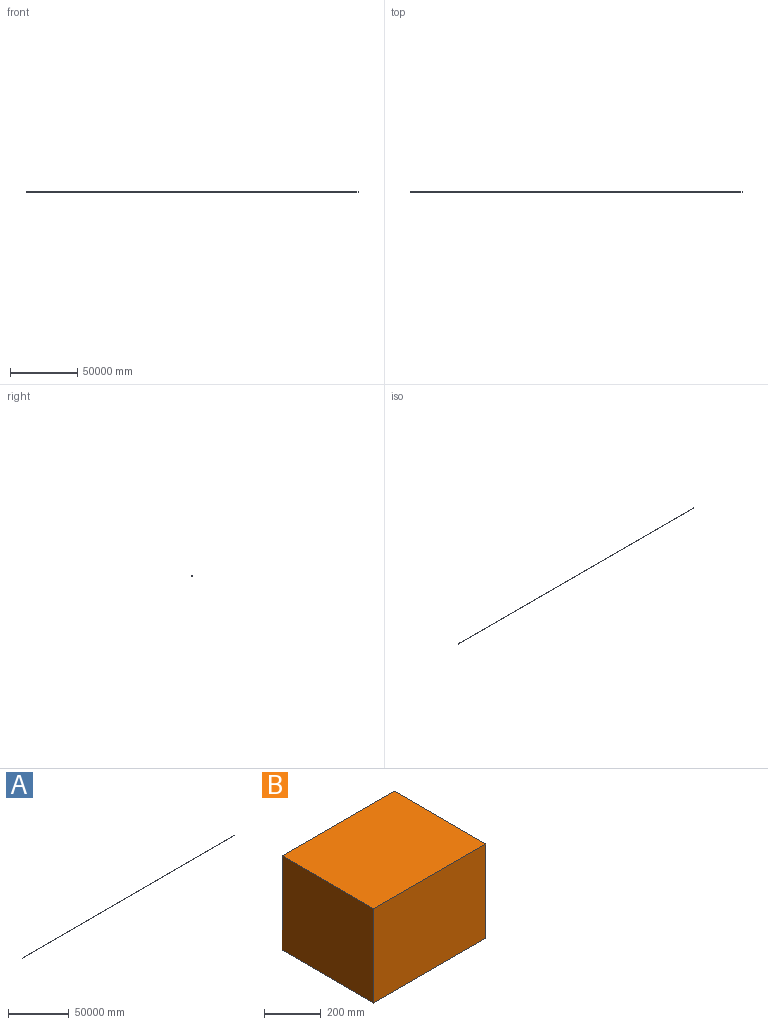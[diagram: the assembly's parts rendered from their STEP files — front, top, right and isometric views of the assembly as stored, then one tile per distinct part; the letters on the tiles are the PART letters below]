
ASSEMBLY  parts=2 mates=1
PART A: 6 faces, bbox 246583.2x167.6x127 mm
  f0: plane 246583.2x167.64mm, normal (0,0,1), area 41337207.6mm2, adj f1,f3,f4,f5
  f1: plane 246583.2x127mm, normal (0,-1,0), area 31316066.4mm2, adj f0,f2,f4,f5
  f2: plane 246583.2x167.64mm, normal (0,0,-1), area 41337207.6mm2, adj f1,f3,f4,f5
  f3: plane 246583.2x127mm, normal (0,1,0), area 31316066.4mm2, adj f0,f2,f4,f5
  f4: plane 167.64x127mm, normal (1,0,0), area 21290.3mm2, adj f0,f1,f2,f3
  f5: plane 167.64x127mm, normal (-1,0,0), area 21290.3mm2, adj f0,f1,f2,f3
PART B: 6 faces, bbox 558.8x457.2x406.4 mm
  f0: plane 558.8x406.4mm, normal (0,1,0), area 227096.3mm2, adj f1,f3,f4,f5
  f1: plane 558.8x457.2mm, normal (0,0,1), area 255483.4mm2, adj f0,f2,f4,f5
  f2: plane 558.8x406.4mm, normal (0,-1,0), area 227096.3mm2, adj f1,f3,f4,f5
  f3: plane 558.8x457.2mm, normal (0,0,-1), area 255483.4mm2, adj f0,f2,f4,f5
  f4: plane 457.2x406.4mm, normal (-1,0,0), area 185806.1mm2, adj f0,f1,f2,f3
  f5: plane 457.2x406.4mm, normal (1,0,0), area 185806.1mm2, adj f0,f1,f2,f3
PLACE A t=(-21560,43240.22,-23179.59)mm
PLACE B t=(-21560,43552.64,-23319.29)mm
MATE fastened B.f5 <-> A.f5  axis (1,0,0) through (-21560,43324.04,-23116.09)mm
